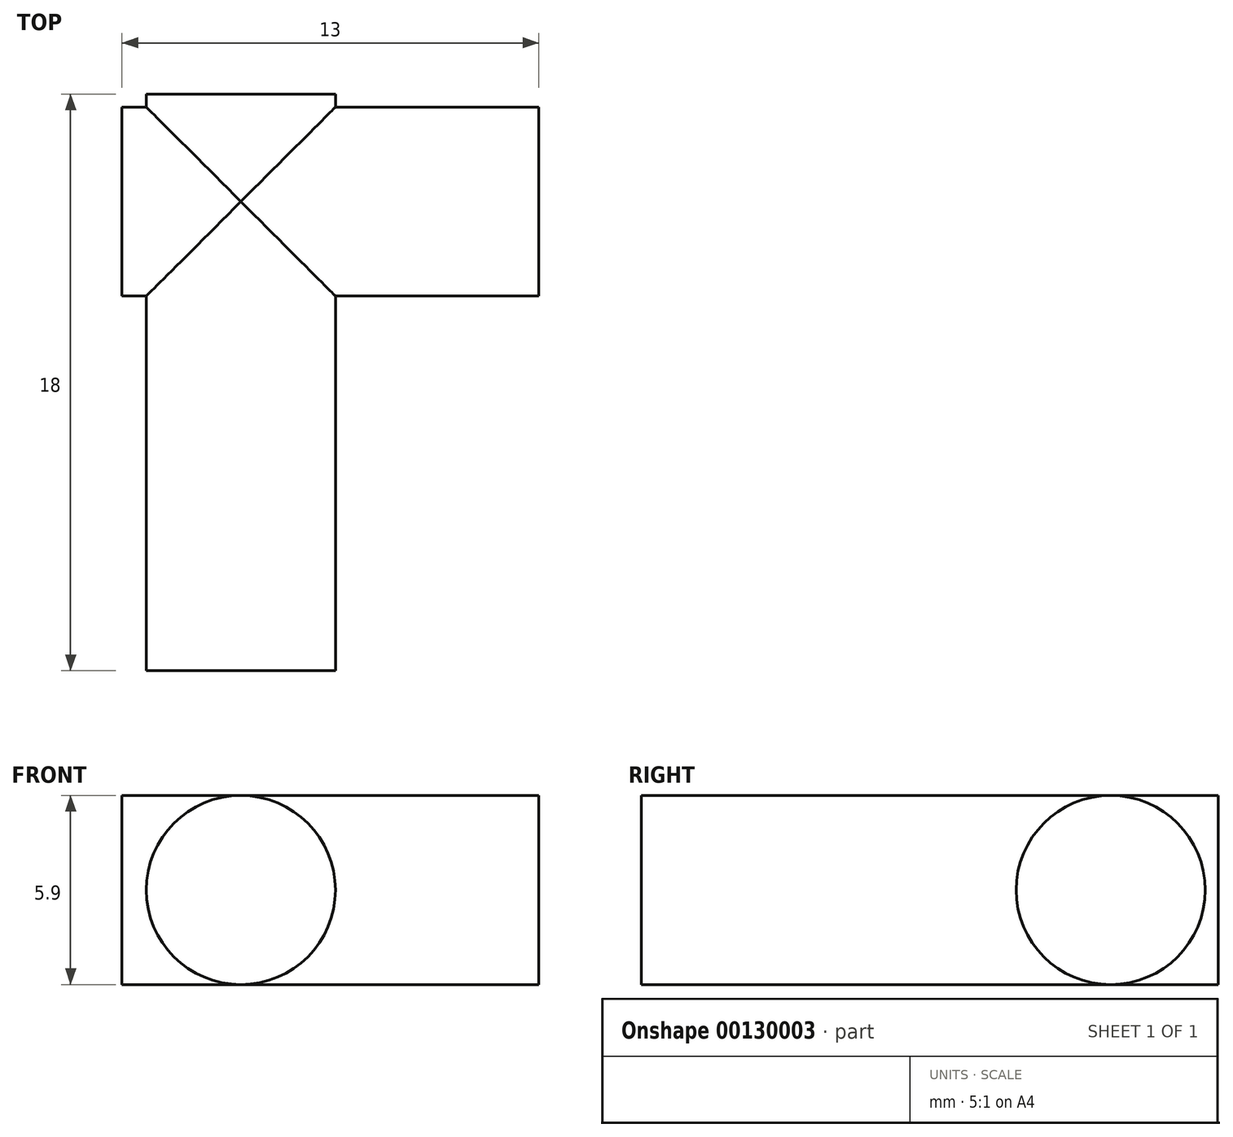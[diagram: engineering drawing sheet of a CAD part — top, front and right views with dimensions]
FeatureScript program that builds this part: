
annotation { "Feature Type Name" : "Feature", "Feature Type Description" : "" }
export const myFeature = defineFeature(function(context is Context, id is Id, definition is map)
    precondition{}
    {
        {
            var Q0;
            Q0=qCreatedBy(makeId("Right.planeOp"),FACE);
            var sketch = newSketch(context, id + "F0", { "sketchPlane" : qUnion([Q0])});
            skCircle(sketch, "E0", {"center": v(-3.36, 0) * mm, "radius": 2.95 * mm});
            skSolve(sketch);
        }
        {
            var Q0;
            Q0=qCreatedBy(makeId("Front.planeOp"),FACE);
            var sketch = newSketch(context, id + "F1", { "sketchPlane" : qUnion([Q0])});
            skCircle(sketch, "E1", {"center": v(3.7, 0) * mm, "radius": 2.95 * mm});
            skSolve(sketch);
        }
        {
            var Q0;
            Q0 = qSketchRegion(id + "F0", true);
            extrude(context, id + "F2", {"entities" : qUnion([Q0]), "depth" : 13 * mm});
        }
        {
            var Q0;
            Q0 = qSketchRegion(id + "F1", true);
            extrude(context, id + "F3", {"entities" : qUnion([Q0]), "operationType" : NewBodyOperationType.ADD, "depth" : 18 * mm});
        }
    });
